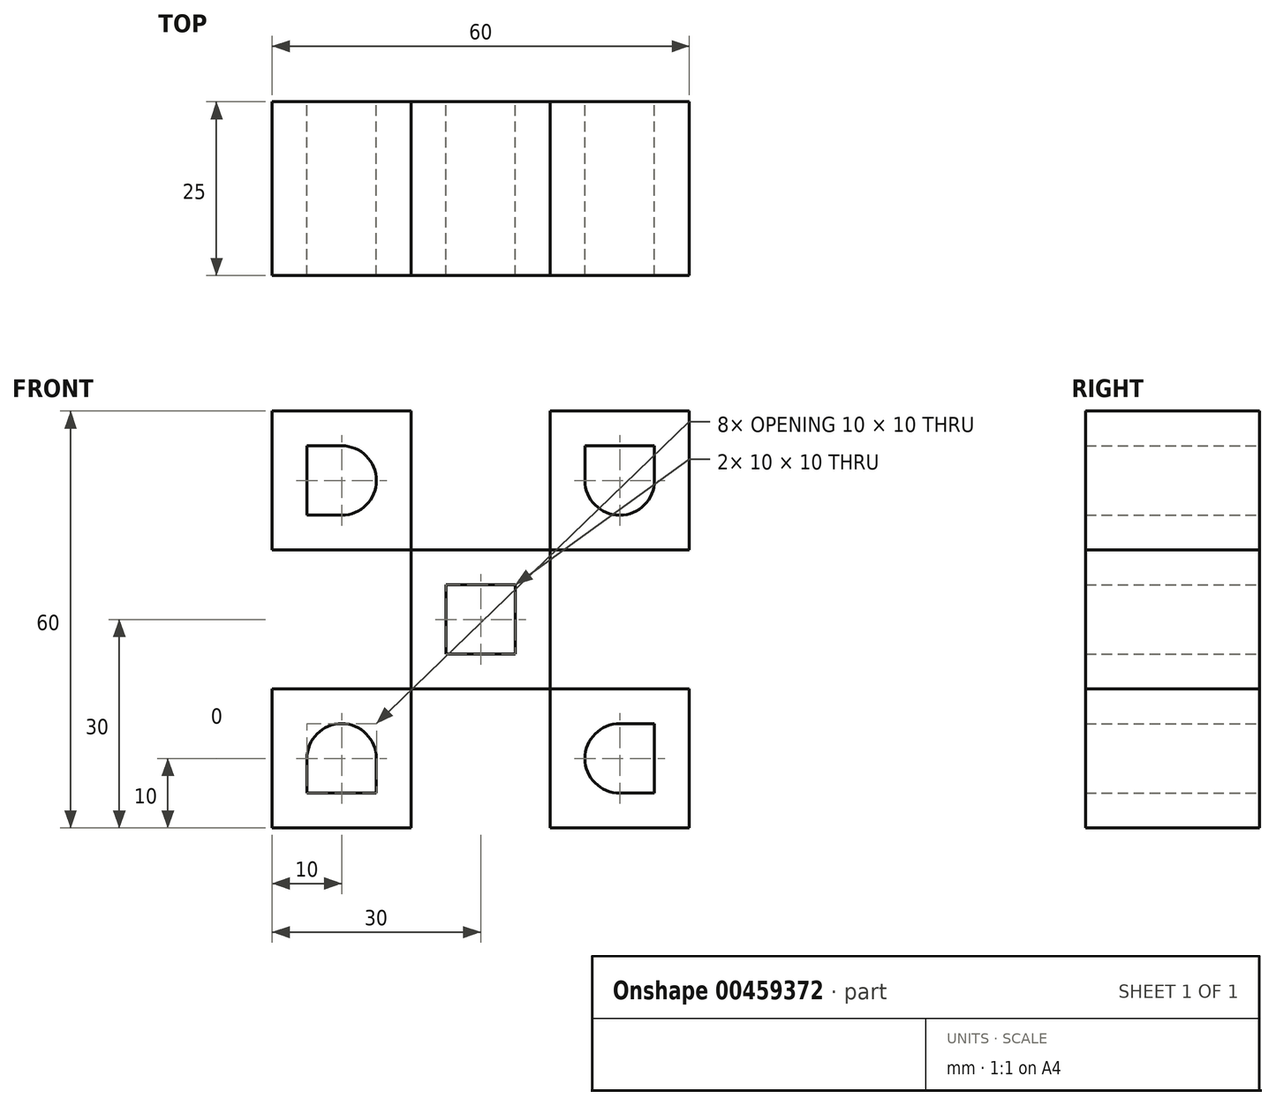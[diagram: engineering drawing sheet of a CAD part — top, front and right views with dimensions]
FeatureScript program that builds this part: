
annotation { "Feature Type Name" : "Feature", "Feature Type Description" : "" }
export const myFeature = defineFeature(function(context is Context, id is Id, definition is map)
    precondition{}
    {
        {
            var Q0;
            Q0=qCreatedBy(makeId("Front.planeOp"),FACE);
            var sketch = newSketch(context, id + "F0", { "sketchPlane" : qUnion([Q0])});
            skLineSegment(sketch, "E0.right", {"start": v(443.39, 0) * mm, "end": v(443.39, 17.46) * mm});
            skLineSegment(sketch, "E1.bottom", {"start": v(0, 0) * mm, "end": v(20, 0) * mm});
            skLineSegment(sketch, "E1.top", {"start": v(0, 20) * mm, "end": v(20, 20) * mm});
            skLineSegment(sketch, "E1.left", {"start": v(0, 0) * mm, "end": v(0, 20) * mm});
            skLineSegment(sketch, "E1.right", {"start": v(20, 0) * mm, "end": v(20, 20) * mm});
            skLineSegment(sketch, "E2.bottom", {"start": v(20, 20) * mm, "end": v(40, 20) * mm});
            skLineSegment(sketch, "E2.top", {"start": v(20, 40) * mm, "end": v(40, 40) * mm});
            skLineSegment(sketch, "E2.left", {"start": v(20, 20) * mm, "end": v(20, 40) * mm});
            skLineSegment(sketch, "E2.right", {"start": v(40, 20) * mm, "end": v(40, 40) * mm});
            skLineSegment(sketch, "E3.bottom", {"start": v(20, 0) * mm, "end": v(40, 0) * mm});
            skLineSegment(sketch, "E3.top", {"start": v(20, -20) * mm, "end": v(40, -20) * mm});
            skLineSegment(sketch, "E3.left", {"start": v(20, 0) * mm, "end": v(20, -20) * mm});
            skLineSegment(sketch, "E3.right", {"start": v(40, 0) * mm, "end": v(40, -20) * mm});
            skLineSegment(sketch, "E4.bottom", {"start": v(0, 20) * mm, "end": v(-20, 20) * mm});
            skLineSegment(sketch, "E4.top", {"start": v(0, 40) * mm, "end": v(-20, 40) * mm});
            skLineSegment(sketch, "E4.left", {"start": v(0, 20) * mm, "end": v(0, 40) * mm});
            skLineSegment(sketch, "E4.right", {"start": v(-20, 20) * mm, "end": v(-20, 40) * mm});
            skLineSegment(sketch, "E5.bottom", {"start": v(0, 0) * mm, "end": v(-20, 0) * mm});
            skLineSegment(sketch, "E5.top", {"start": v(0, -20) * mm, "end": v(-20, -20) * mm});
            skLineSegment(sketch, "E5.left", {"start": v(0, 0) * mm, "end": v(0, -20) * mm});
            skLineSegment(sketch, "E5.right", {"start": v(-20, 0) * mm, "end": v(-20, -20) * mm});
            skLineSegment(sketch, "E6.bottom", {"start": v(15, 15) * mm, "end": v(5, 15) * mm});
            skLineSegment(sketch, "E6.top", {"start": v(15, 5) * mm, "end": v(5, 5) * mm});
            skLineSegment(sketch, "E6.left", {"start": v(15, 15) * mm, "end": v(15, 5) * mm});
            skLineSegment(sketch, "E6.right", {"start": v(5, 15) * mm, "end": v(5, 5) * mm});
            skPoint(sketch, "E6.middle", {"position": v(10, 10) * mm});
            skPoint(sketch, "E6.middle.positionSnap0", {"position": v(20, 10) * mm});
            skPoint(sketch, "E6.middle.positionSnap1", {"position": v(10, 20) * mm});
            skPoint(sketch, "E6.centerSnap0", {"position": v(20, 10) * mm});
            skPoint(sketch, "E6.centerSnap1", {"position": v(10, 20) * mm});
            skLineSegment(sketch, "E7.top", {"start": v(35, 35) * mm, "end": v(25, 35) * mm});
            skLineSegment(sketch, "E7.left", {"start": v(35, 30) * mm, "end": v(35, 35) * mm});
            skLineSegment(sketch, "E7.right", {"start": v(25, 30) * mm, "end": v(25, 35) * mm});
            skPoint(sketch, "E7.middle", {"position": v(30, 30) * mm});
            skPoint(sketch, "E7.middle.positionSnap0", {"position": v(40, 30) * mm});
            skPoint(sketch, "E7.middle.positionSnap1", {"position": v(30, 40) * mm});
            skPoint(sketch, "E7.centerSnap0", {"position": v(40, 30) * mm});
            skPoint(sketch, "E7.centerSnap1", {"position": v(30, 40) * mm});
            skLineSegment(sketch, "E8.bottom", {"start": v(35, -15) * mm, "end": v(30, -15) * mm});
            skLineSegment(sketch, "E8.top", {"start": v(35, -5) * mm, "end": v(30, -5) * mm});
            skLineSegment(sketch, "E8.left", {"start": v(35, -15) * mm, "end": v(35, -5) * mm});
            skPoint(sketch, "E8.middle", {"position": v(30, -10) * mm});
            skPoint(sketch, "E8.middle.positionSnap0", {"position": v(40, -10) * mm});
            skPoint(sketch, "E8.middle.positionSnap1", {"position": v(30, 0) * mm});
            skPoint(sketch, "E8.centerSnap0", {"position": v(40, -10) * mm});
            skPoint(sketch, "E8.centerSnap1", {"position": v(30, 0) * mm});
            skLineSegment(sketch, "E9.bottom", {"start": v(-5, -15) * mm, "end": v(-15, -15) * mm});
            skLineSegment(sketch, "E9.left", {"start": v(-5, -15) * mm, "end": v(-5, -10) * mm});
            skLineSegment(sketch, "E9.right", {"start": v(-15, -15) * mm, "end": v(-15, -10) * mm});
            skPoint(sketch, "E9.middle", {"position": v(-10, -10) * mm});
            skPoint(sketch, "E9.middle.positionSnap0", {"position": v(0, -10) * mm});
            skPoint(sketch, "E9.middle.positionSnap1", {"position": v(-10, 0) * mm});
            skPoint(sketch, "E9.centerSnap0", {"position": v(0, -10) * mm});
            skPoint(sketch, "E9.centerSnap1", {"position": v(-10, 0) * mm});
            skLineSegment(sketch, "E10.bottom", {"start": v(-10, 25) * mm, "end": v(-15, 25) * mm});
            skLineSegment(sketch, "E10.top", {"start": v(-10, 35) * mm, "end": v(-15, 35) * mm});
            skLineSegment(sketch, "E10.right", {"start": v(-15, 25) * mm, "end": v(-15, 35) * mm});
            skPoint(sketch, "E10.middle", {"position": v(-10, 30) * mm});
            skPoint(sketch, "E10.middle.positionSnap0", {"position": v(0, 30) * mm});
            skPoint(sketch, "E10.middle.positionSnap1", {"position": v(-10, 40) * mm});
            skPoint(sketch, "E10.centerSnap0", {"position": v(0, 30) * mm});
            skPoint(sketch, "E10.centerSnap1", {"position": v(-10, 40) * mm});
            skArc(sketch, "E11", {"start": v(-10, 25) * mm, "mid": v(-5, 30) * mm, "end": v(-10, 35) * mm});
            skArc(sketch, "E12", {"start": v(25, 30) * mm, "mid": v(30, 25) * mm, "end": v(35, 30) * mm});
            skArc(sketch, "E13", {"start": v(-5, -10) * mm, "mid": v(-10, -5) * mm, "end": v(-15, -10) * mm});
            skArc(sketch, "E14", {"start": v(30, -5) * mm, "mid": v(25, -10) * mm, "end": v(30, -15) * mm});
            skPoint(sketch, "E15.orphan", {"position": v(-5, 35) * mm});
            skPoint(sketch, "E16.orphan", {"position": v(-5, 25) * mm});
            skPoint(sketch, "E17.orphan", {"position": v(25, 25) * mm});
            skPoint(sketch, "E7.bottom.start.orphan", {"position": v(35, 25) * mm});
            skPoint(sketch, "E18.orphan", {"position": v(-15, -5) * mm});
            skPoint(sketch, "E19.orphan", {"position": v(-5, -5) * mm});
            skPoint(sketch, "E20.orphan", {"position": v(25, -5) * mm});
            skPoint(sketch, "E21.orphan", {"position": v(25, -15) * mm});
            skSolve(sketch);
        }
        {
            var Q0;
            Q0=makeQuery(id+"F0.imprint","IMPRINT",FACE,{"disambiguationData":[TD([[makeQuery(id+"F0.imprint","IMPRINT",EDGE,{"derivedFrom":sQuery(id+"F0.wireOp",EDGE,"E1.bottom")}),1.0]])]});
            var Q1;
            Q1=makeQuery(id+"F0.imprint","IMPRINT",FACE,{"disambiguationData":[TD([[makeQuery(id+"F0.imprint","IMPRINT",EDGE,{"derivedFrom":sQuery(id+"F0.wireOp",EDGE,"E3.bottom")}),-1.0]])]});
            var Q2;
            Q2=makeQuery(id+"F0.imprint","IMPRINT",FACE,{"disambiguationData":[TD([[makeQuery(id+"F0.imprint","IMPRINT",EDGE,{"derivedFrom":sQuery(id+"F0.wireOp",EDGE,"E4.bottom")}),-1.0]])]});
            var Q3;
            Q3=makeQuery(id+"F0.imprint","IMPRINT",FACE,{"disambiguationData":[TD([[makeQuery(id+"F0.imprint","IMPRINT",EDGE,{"derivedFrom":sQuery(id+"F0.wireOp",EDGE,"E5.bottom")}),1.0]])]});
            var Q4;
            Q4=makeQuery(id+"F0.imprint","IMPRINT",FACE,{"disambiguationData":[TD([[makeQuery(id+"F0.imprint","IMPRINT",EDGE,{"derivedFrom":sQuery(id+"F0.wireOp",EDGE,"E2.bottom")}),1.0]])]});
            extrude(context, id + "F1", {"entities" : qUnion([Q0, Q1, Q2, Q3, Q4]), "depth" : 25 * mm});
        }
        {
            var Q0;
            Q0 = qSketchRegion(id + "F0", true);
            extrude(context, id + "F2", {"entities" : qUnion([Q0]), "depth" : 25 * mm});
        }
    });
